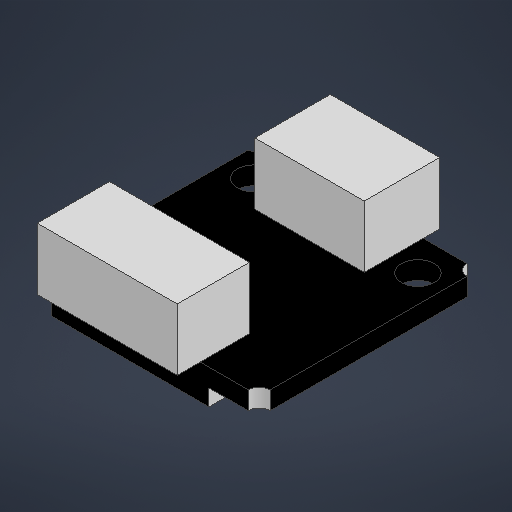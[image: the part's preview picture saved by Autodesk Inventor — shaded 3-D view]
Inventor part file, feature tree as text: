
AUTODESK INVENTOR PART (.ipt)
format: ipt  version: 2025.1 (Build 291241000, 241)  size: 256,512 bytes
history: native  units: mm
features: extrude x4, sketch x4, fillet x1, shell x1, projected_geometry x1
ambient origin geometry x8: Origin, YZ Plane, XZ Plane, XY Plane, X Axis, Y Axis, Z Axis, Center Point
bodies: Solid1 (feature_tree)
feature tree (11):
  extrude  "Extrusion1"  Depth=20.0mm
  extrude  "Extrusion2"  Depth=15.0mm
  extrude  "Extrusion3"  Depth=1.65mm TaperAngle=0.0deg
  fillet  "Fillet1"  Radius=10.0mm
  extrude  "Extrusion4"  Depth=1.5mm
  shell  "Shell1"  Thickness=5.65mm
  sketch  "Sketch1"  dims[d0=20.0mm d1=20.0mm]
  sketch  "Sketch2"  dims[d2=15.0mm d3=3.0mm]
  projected_geometry  "Projected Loop1"
  sketch  "Sketch3"  dims[d4=3.0mm d5=1.65mm d6=0.0mm d7=10.0mm]
  sketch  "Sketch4"  dims[d8=6.9mm d9=1.5mm d10=5.65mm d11=0.0mm d12=1.8mm d13=12.8mm d14=6.6mm d15=2.1mm d16=5.65mm d17=0.0mm d18=1.0mm d19=6.2mm d20=6.2mm d21=4.4mm d22=1.0mm d23=4.6mm d24=8.2mm d25=1.5mm d26=0.0mm d27=1.0mm]
